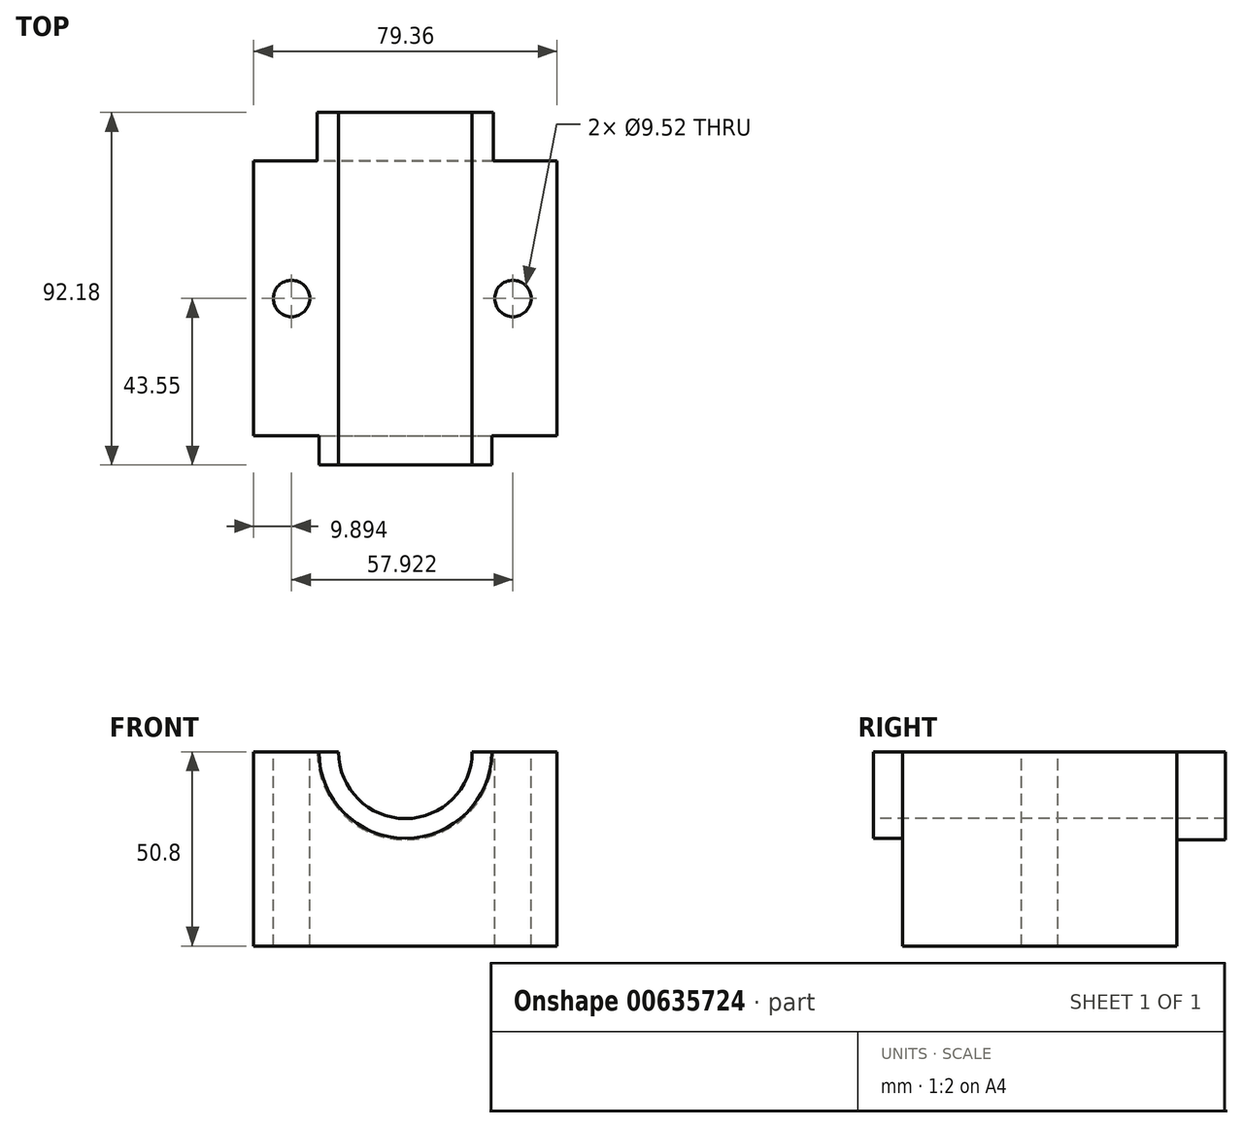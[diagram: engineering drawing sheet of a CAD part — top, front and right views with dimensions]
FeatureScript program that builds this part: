
annotation { "Feature Type Name" : "Feature", "Feature Type Description" : "" }
export const myFeature = defineFeature(function(context is Context, id is Id, definition is map)
    precondition{}
    {
        {
            var Q0;
            Q0=qCreatedBy(makeId("Top.planeOp"),FACE);
            var sketch = newSketch(context, id + "F0", { "sketchPlane" : qUnion([Q0])});
            skLineSegment(sketch, "E0.bottom", {"start": v(-39.68, 35.93) * mm, "end": v(39.68, 35.93) * mm});
            skLineSegment(sketch, "E0.top", {"start": v(-39.68, -35.93) * mm, "end": v(39.68, -35.93) * mm});
            skLineSegment(sketch, "E0.left", {"start": v(-39.68, 35.93) * mm, "end": v(-39.68, -35.93) * mm});
            skLineSegment(sketch, "E0.right", {"start": v(39.68, 35.93) * mm, "end": v(39.68, -35.93) * mm});
            skPoint(sketch, "E0.middle", {"position": v(0, 0) * mm});
            skSolve(sketch);
        }
        {
            var Q0;
            Q0=makeQuery(id+"F0.imprint","IMPRINT",FACE,{"disambiguationData":[TD([[makeQuery(id+"F0.imprint","IMPRINT",EDGE,{"derivedFrom":sQuery(id+"F0.wireOp",EDGE,"E0.bottom")}),-1.0]])]});
            extrude(context, id + "F1", {"entities" : qUnion([Q0]), "depth" : 25.4 * mm, "offsetDistance" : 25.4 * mm});
        }
        {
            var Q0;
            Q0=makeQuery(id+"F1.opExtrude","CAP_FACE",FACE,{"disambiguationData":[OSD([sQuery(id+"F0.wireOp",EDGE,"E0.bottom"),sQuery(id+"F0.wireOp",EDGE,"E0.top"),sQuery(id+"F0.wireOp",EDGE,"E0.left"),sQuery(id+"F0.wireOp",EDGE,"E0.right")])],"isStart":false});
            extrude(context, id + "F2", {"entities" : qUnion([Q0]), "operationType" : NewBodyOperationType.ADD, "depth" : 25.4 * mm, "offsetDistance" : 25.4 * mm});
        }
        {
            var Q0;
            {var subQ0=sQuery(id+"F0.wireOp",EDGE,"E0.top");Q0=makeQuery(id+"F2.boolean.opBoolean","MERGE",FACE,{"derivedFrom":[makeQuery(id+"F1.opExtrude","SWEPT_FACE",FACE,{"disambiguationData":[OSD([subQ0])]}),makeQuery(id+"F2.opExtrude","SWEPT_FACE",FACE,{"disambiguationData":[OSD([subQ0])]})]});}
            var sketch = newSketch(context, id + "F3", { "sketchPlane" : qUnion([Q0])});
            skCircle(sketch, "E1", {"center": v(0, 50.8) * mm, "radius": 22 * mm});
            skCircle(sketch, "E2", {"center": v(0, 50.8) * mm, "radius": 17.47 * mm});
            skSolve(sketch);
        }
        {
            var Q0;
            {var subQ0=sQuery(id+"F3.wireOp",EDGE,"E2");var subQ1=makeQuery(id+"F2.opExtrude","CAP_EDGE",EDGE,{"disambiguationData":[OSD([sQuery(id+"F0.wireOp",EDGE,"E0.top")])],"isStart":false});var subQ2=makeQuery(id+"F3.imprint","INTERSECT",VERTEX,{"disambiguationData":[OD(0.0)],"derivedFrom":[subQ1,subQ0]});Q0=makeQuery(id+"F3.imprint","IMPRINT",FACE,{"disambiguationData":[TD([[makeQuery(id+"F3.imprint","IMPRINT",EDGE,{"disambiguationData":[TD([[subQ2,-1.0]])],"derivedFrom":subQ0}),1.0]])]});}
            extrude(context, id + "F4", {"entities" : qUnion([Q0]), "operationType" : NewBodyOperationType.REMOVE, "oppositeDirection" : true, "depth" : 101.6 * mm, "offsetDistance" : 25.4 * mm});
        }
        {
            var Q0;
            {var subQ0=sQuery(id+"F0.wireOp",EDGE,"E0.bottom");var subQ1=sQuery(id+"F0.wireOp",EDGE,"E0.top");var subQ2=sQuery(id+"F0.wireOp",EDGE,"E0.right");Q0=makeQuery(id+"F4.boolean.opBoolean","SPLIT",FACE,{"disambiguationData":[TD([makeQuery(id+"F1.opExtrude","SWEPT_FACE",FACE,{"disambiguationData":[OSD([subQ2])]})])],"derivedFrom":makeQuery(id+"F2.opExtrude","CAP_FACE",FACE,{"disambiguationData":[OSD([subQ0,subQ1,sQuery(id+"F0.wireOp",EDGE,"E0.left"),subQ2])],"isStart":false})});}
            var sketch = newSketch(context, id + "F5", { "sketchPlane" : qUnion([Q0])});
            skCircle(sketch, "E3", {"center": v(28.14, 0) * mm, "radius": 4.76 * mm});
            skPoint(sketch, "E3.centerSnap0", {"position": v(39.68, 0) * mm});
            skCircle(sketch, "E4", {"center": v(-29.79, 0) * mm, "radius": 4.76 * mm});
            skSolve(sketch);
        }
        {
            var Q0;
            Q0=makeQuery(id+"F5.imprint","IMPRINT",FACE,{"disambiguationData":[TD([[makeQuery(id+"F5.imprint","IMPRINT",EDGE,{"derivedFrom":sQuery(id+"F5.wireOp",EDGE,"E4")}),1.0]])]});
            var Q1;
            Q1=makeQuery(id+"F5.imprint","IMPRINT",FACE,{"disambiguationData":[TD([[makeQuery(id+"F5.imprint","IMPRINT",EDGE,{"derivedFrom":sQuery(id+"F5.wireOp",EDGE,"E3")}),1.0]])]});
            extrude(context, id + "F6", {"entities" : qUnion([Q0, Q1]), "operationType" : NewBodyOperationType.ADD, "depth" : 127 * mm, "offsetDistance" : 25.4 * mm});
        }
        {
            var Q0;
            Q0=makeQuery(id+"F6.opExtrude","CAP_FACE",FACE,{"disambiguationData":[OSD([sQuery(id+"F5.wireOp",EDGE,"E3")])],"isStart":false});
            var Q1;
            Q1=makeQuery(id+"F6.opExtrude","CAP_FACE",FACE,{"disambiguationData":[OSD([sQuery(id+"F5.wireOp",EDGE,"E4")])],"isStart":false});
            extrude(context, id + "F7", {"entities" : qUnion([Q0, Q1]), "operationType" : NewBodyOperationType.REMOVE, "oppositeDirection" : true, "depth" : 508 * mm, "offsetDistance" : 25.4 * mm});
        }
        {
            var Q0;
            {var subQ0=sQuery(id+"F0.wireOp",EDGE,"E0.top");Q0=makeQuery(id+"F2.boolean.opBoolean","MERGE",FACE,{"derivedFrom":[makeQuery(id+"F1.opExtrude","SWEPT_FACE",FACE,{"disambiguationData":[OSD([subQ0])]}),makeQuery(id+"F2.opExtrude","SWEPT_FACE",FACE,{"disambiguationData":[OSD([subQ0])]})]});}
            var sketch = newSketch(context, id + "F8", { "sketchPlane" : qUnion([Q0])});
            skArc(sketch, "E5", {"start": v(-22.61, 50.8) * mm, "mid": v(0, 28.19) * mm, "end": v(22.61, 50.8) * mm});
            skLineSegment(sketch, "E6", {"start": v(22.61, 50.8) * mm, "end": v(-22.61, 50.8) * mm});
            skSolve(sketch);
        }
        {
            var Q0;
            {var subQ0=sQuery(id+"F8.wireOp",EDGE,"E5");Q0=makeQuery(id+"F8.imprint","IMPRINT",FACE,{"disambiguationData":[TD([[makeQuery(id+"F8.imprint","IMPRINT",EDGE,{"derivedFrom":subQ0}),1.0]])]});}
            extrude(context, id + "F9", {"entities" : qUnion([Q0]), "operationType" : NewBodyOperationType.ADD, "depth" : 7.62 * mm, "offsetDistance" : 25.4 * mm});
        }
        {
            var Q0;
            {var subQ0=sQuery(id+"F0.wireOp",EDGE,"E0.bottom");Q0=makeQuery(id+"F2.boolean.opBoolean","MERGE",FACE,{"derivedFrom":[makeQuery(id+"F1.opExtrude","SWEPT_FACE",FACE,{"disambiguationData":[OSD([subQ0])]}),makeQuery(id+"F2.opExtrude","SWEPT_FACE",FACE,{"disambiguationData":[OSD([subQ0])]})]});}
            var sketch = newSketch(context, id + "F10", { "sketchPlane" : qUnion([Q0])});
            skArc(sketch, "E7", {"start": v(-23.06, 50.8) * mm, "mid": v(0, 27.74) * mm, "end": v(23.06, 50.8) * mm});
            skSolve(sketch);
        }
        {
            var Q0;
            {var subQ0=sQuery(id+"F10.wireOp",EDGE,"E7");Q0=makeQuery(id+"F10.imprint","IMPRINT",FACE,{"disambiguationData":[TD([[makeQuery(id+"F10.imprint","IMPRINT",EDGE,{"derivedFrom":subQ0}),1.0]])]});}
            extrude(context, id + "F11", {"entities" : qUnion([Q0]), "operationType" : NewBodyOperationType.ADD, "depth" : 25.4 * mm, "offsetDistance" : 25.4 * mm});
        }
        {
            var Q0;
            Q0=makeQuery(id+"F11.opExtrude","CAP_FACE",FACE,{"disambiguationData":[OSD([sQuery(id+"F0.wireOp",EDGE,"E0.bottom"),sQuery(id+"F3.wireOp",EDGE,"E2"),sQuery(id+"F10.wireOp",EDGE,"E7")])],"isStart":false});
            extrude(context, id + "F12", {"entities" : qUnion([Q0]), "operationType" : NewBodyOperationType.REMOVE, "oppositeDirection" : true, "depth" : 12.7 * mm, "offsetDistance" : 25.4 * mm});
        }
    });
